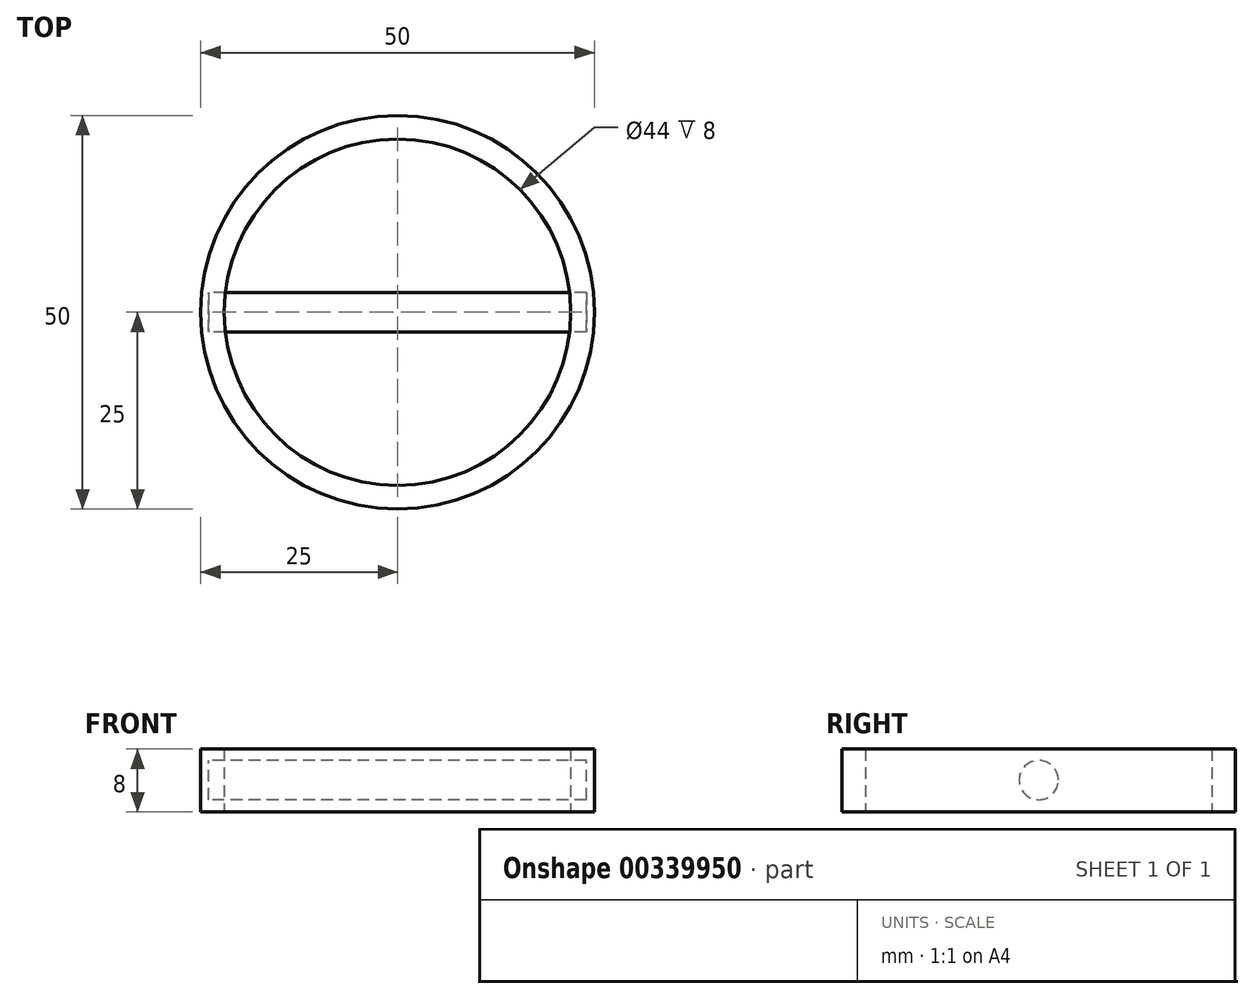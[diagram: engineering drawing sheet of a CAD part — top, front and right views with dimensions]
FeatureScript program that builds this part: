
annotation { "Feature Type Name" : "Feature", "Feature Type Description" : "" }
export const myFeature = defineFeature(function(context is Context, id is Id, definition is map)
    precondition{}
    {
        {
            var Q0;
            Q0=qCreatedBy(makeId("Top.planeOp"),FACE);
            var sketch = newSketch(context, id + "F0", { "sketchPlane" : qUnion([Q0])});
            skCircle(sketch, "E0", {"center": v(0, 0) * mm, "radius": 25 * mm});
            skCircle(sketch, "E1", {"center": v(0, 0) * mm, "radius": 22 * mm});
            skSolve(sketch);
        }
        {
            var Q0;
            Q0 = qSketchRegion(id + "F0", true);
            extrude(context, id + "F1", {"entities" : qUnion([Q0]), "depth" : 8 * mm, "offsetDistance" : 25 * mm});
        }
        {
            var Q0;
            Q0=qCreatedBy(makeId("Right.planeOp"),FACE);
            var sketch = newSketch(context, id + "F2", { "sketchPlane" : qUnion([Q0])});
            skCircle(sketch, "E2", {"center": v(0, 4.07) * mm, "radius": 2.5 * mm});
            skSolve(sketch);
        }
        {
            var Q0;
            Q0 = qSketchRegion(id + "F2", true);
            extrude(context, id + "F3", {"entities" : qUnion([Q0]), "depth" : 24 * mm, "offsetDistance" : 25 * mm, "hasSecondDirection" : true, "secondDirectionOppositeDirection" : true, "secondDirectionDepth" : 24 * mm});
        }
    });
